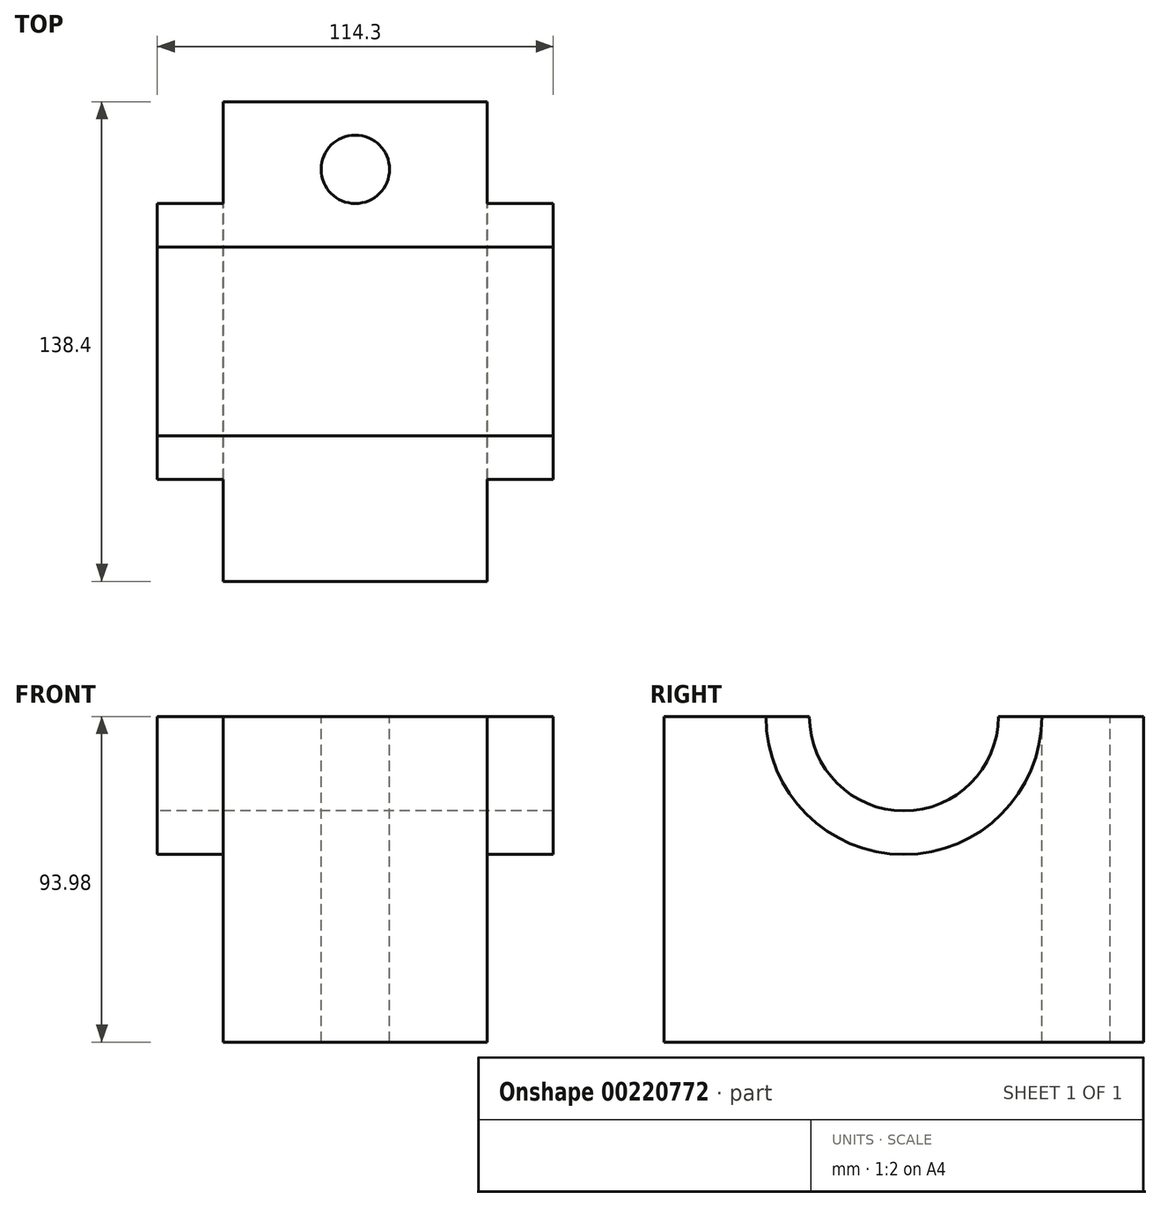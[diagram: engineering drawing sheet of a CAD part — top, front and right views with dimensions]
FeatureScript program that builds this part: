
annotation { "Feature Type Name" : "Feature", "Feature Type Description" : "" }
export const myFeature = defineFeature(function(context is Context, id is Id, definition is map)
    precondition{}
    {
        {
            var Q0;
            Q0=qCreatedBy(makeId("Right.planeOp"),FACE);
            var sketch = newSketch(context, id + "F0", { "sketchPlane" : qUnion([Q0])});
            skLineSegment(sketch, "E0.bottom", {"start": v(69.2, -46.99) * mm, "end": v(-69.2, -46.99) * mm});
            skLineSegment(sketch, "E0.top", {"start": v(69.2, 46.99) * mm, "end": v(-69.2, 46.99) * mm});
            skLineSegment(sketch, "E0.left", {"start": v(69.2, -46.99) * mm, "end": v(69.2, 46.99) * mm});
            skLineSegment(sketch, "E0.right", {"start": v(-69.2, -46.99) * mm, "end": v(-69.2, 46.99) * mm});
            skSolve(sketch);
        }
        {
            var Q0;
            Q0=makeQuery(id+"F0.imprint","IMPRINT",FACE,{"disambiguationData":[TD([[makeQuery(id+"F0.imprint","IMPRINT",EDGE,{"derivedFrom":sQuery(id+"F0.wireOp",EDGE,"E0.bottom")}),-1.0]])]});
            extrude(context, id + "F1", {"entities" : qUnion([Q0]), "endBound" : BoundingType.SYMMETRIC, "depth" : 76.2 * mm});
        }
        {
            var Q0;
            Q0=qCreatedBy(makeId("Right.planeOp"),FACE);
            var sketch = newSketch(context, id + "F2", { "sketchPlane" : qUnion([Q0])});
            skArc(sketch, "E1", {"start": v(-39.83, 46.99) * mm, "mid": v(0, 7.16) * mm, "end": v(39.83, 46.99) * mm});
            skLineSegment(sketch, "E2", {"start": v(-39.83, 46.99) * mm, "end": v(39.83, 46.99) * mm});
            skSolve(sketch);
        }
        {
            var Q0;
            Q0 = qSketchRegion(id + "F2", true);
            extrude(context, id + "F3", {"entities" : qUnion([Q0]), "operationType" : NewBodyOperationType.ADD, "endBound" : BoundingType.SYMMETRIC, "depth" : 114.3 * mm});
        }
        {
            var Q0;
            Q0=qCreatedBy(makeId("Right.planeOp"),FACE);
            var sketch = newSketch(context, id + "F4", { "sketchPlane" : qUnion([Q0])});
            skCircle(sketch, "E3", {"center": v(0, 46.99) * mm, "radius": 27.27 * mm});
            skSolve(sketch);
        }
        {
            var Q0;
            Q0 = qSketchRegion(id + "F4", true);
            extrude(context, id + "F5", {"entities" : qUnion([Q0]), "operationType" : NewBodyOperationType.REMOVE, "endBound" : BoundingType.SYMMETRIC, "depth" : 127 * mm});
        }
        {
            var Q0;
            {var subQ0=sQuery(id+"F0.wireOp",EDGE,"E0.left");var subQ1=sQuery(id+"F2.wireOp",EDGE,"E2");var subQ4=sQuery(id+"F0.wireOp",EDGE,"E0.top");Q0=makeQuery(id+"F5.boolean.opBoolean","SPLIT",FACE,{"disambiguationData":[TD([makeQuery(id+"F1.opExtrude","SWEPT_FACE",FACE,{"disambiguationData":[OSD([subQ0])]})])],"derivedFrom":makeQuery(id+"F3.boolean.opBoolean","MERGE",FACE,{"derivedFrom":[makeQuery(id+"F1.opExtrude","SWEPT_FACE",FACE,{"disambiguationData":[OSD([subQ4])]}),makeQuery(id+"F3.opExtrude","SWEPT_FACE",FACE,{"disambiguationData":[OSD([subQ1])]})]})});}
            var sketch = newSketch(context, id + "F6", { "sketchPlane" : qUnion([Q0])});
            skCircle(sketch, "E4", {"center": v(0, 49.7) * mm, "radius": 9.87 * mm});
            skCircle(sketch, "E5.MirrorC", {"center": v(0, -49.7) * mm, "radius": 9.87 * mm});
            skSolve(sketch);
        }
        {
            var Q0;
            Q0=makeQuery(id+"F6.imprint","IMPRINT",FACE,{"disambiguationData":[TD([[makeQuery(id+"F6.imprint","IMPRINT",EDGE,{"derivedFrom":sQuery(id+"F6.wireOp",EDGE,"E4")}),1.0]])]});
            var Q1;
            Q1=makeQuery(id+"F6.imprint","IMPRINT",FACE,{"disambiguationData":[TD([[makeQuery(id+"F6.imprint","IMPRINT",EDGE,{"derivedFrom":sQuery(id+"F6.wireOp",EDGE,"E5.MirrorC")}),-1.0]])]});
            extrude(context, id + "F7", {"entities" : qUnion([Q0, Q1]), "operationType" : NewBodyOperationType.REMOVE, "oppositeDirection" : true, "depth" : 203.2 * mm});
        }
    });
